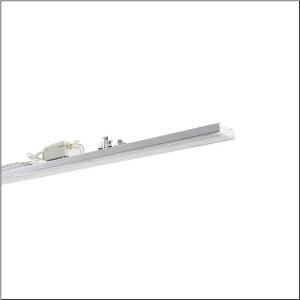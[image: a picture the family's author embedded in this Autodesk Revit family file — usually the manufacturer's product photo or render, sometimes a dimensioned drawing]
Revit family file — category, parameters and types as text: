
# Revit family: licross_11_recessed_mo_51tl14de445g
name_source: partatom
category: Lighting Fixtures
units: mm (PartAtom-declared; Revit-internal decimal feet)

## family parameters
Cut with Voids When Loaded = No
Host = Face
Light Source = No
Part Type = Normal
Room Calculation Point = No
Round Connector Dimension = Use Diameter
Shared = No

## types (1)
- --- (1 x LED, 4710 lm, 29.6 W, 4000K)
    Apparent Load = 30 VA
    CIE Flux Codes = 56 84 97 100 100
    Color Rendering = 80
    Color Temperature = 4000K
    Default Elevation = 1800 mm
    Description = Licross 11 Recessed MO, luminaire insert, of sheet steel, coil coated, white, length: 750mm, width: 66mm, height: 67mm, LED rated luminous flux: 4.710lm, light colour: 840, SDCM (Standard Deviation of Colour Matching)MacAdam ≤ 2 SDCM (initial), control gear: DALI 2, with plug, 5-pole, with phase selection, mains connection: 220..240V, AC, 50/60Hz, rated input power: 30W, internal wiring halogen-free, primary light control with lens, of plastic, primary optical cover: cover, of PMMA, light emission: direct distribution, primary light characteristic: asymmetric, protection rating (complete): IP40, insulation class (complete): insulation class I (protective earthing), certification: CE, ENEC, VDE, UKCA, protection symbol: D if used in an environment without relevant dust loads with corresponding accessories, impact resistance: IK06, permissible ambient temperature for indoor applications: -25..+35°C, corresponds to IFS (International Featured Standards) requirements for safety and quality in the food industry, reducing of maximum allowable ambient temperature of 5°C with ceiling mounting, LABS conformity tested according to VDMA 24364:2018-05, The light source and the operating device comply with the requirements of the Ecodesign Regulation (EU) 2019/2020 and are replaceable in accordance with this regulation, packaging unit: 1 piece
    Height = 58 mm
    Lamp = 1 x LED
    Lamp Light Flux = 4710 lm
    Lamp Power = 29.6 W
    Lamp count = 1
    Length = 750 mm
    Luminous efficacy = 159 lm/W
    Manufacturer = Siteco
    ModVariant = No
    Model = 51TL14DE445G
    Mounting Place = Ceiling
    Mounting Type = Pendant
    Number of Poles = 1
    OnlyDefault = Yes
    Power Factor = 1
    Product Name = Licross 11 Recessed MO
    Product group = luminaire insert | ceiling pendant
    ProductGroupID = 901
    Protection Class = Protection class I
    Protection Degree = IP 40
    RLX_Detail_Level = 1
    RLX_Emergency_Light_Flux = 0 lm
    RLX_Emergency_Type = 0
    RLX_Emergency_Type_DB = No
    RlxData = <blob elided: 29837 chars, md5=d6f1132c>
    Socket = socket
    Standby Power = 0 W
    System Light Flux = 4710 lm
    System Power = 30 W
    Type Comments = factory setting: luminous flux: 100 % | dim-lin: 254 | 378 mA
    Type Image = l_1296930.jpg
    URL = http://relux.com
    VarID = @adj_103037
    Voltage = 0 V
    Weight = 0.00 kg
    Width = 66 mm

## geometry (parser evidence)
native form markers: Blend x4, Sweep x12
no freeform markers — native parametric forms only
